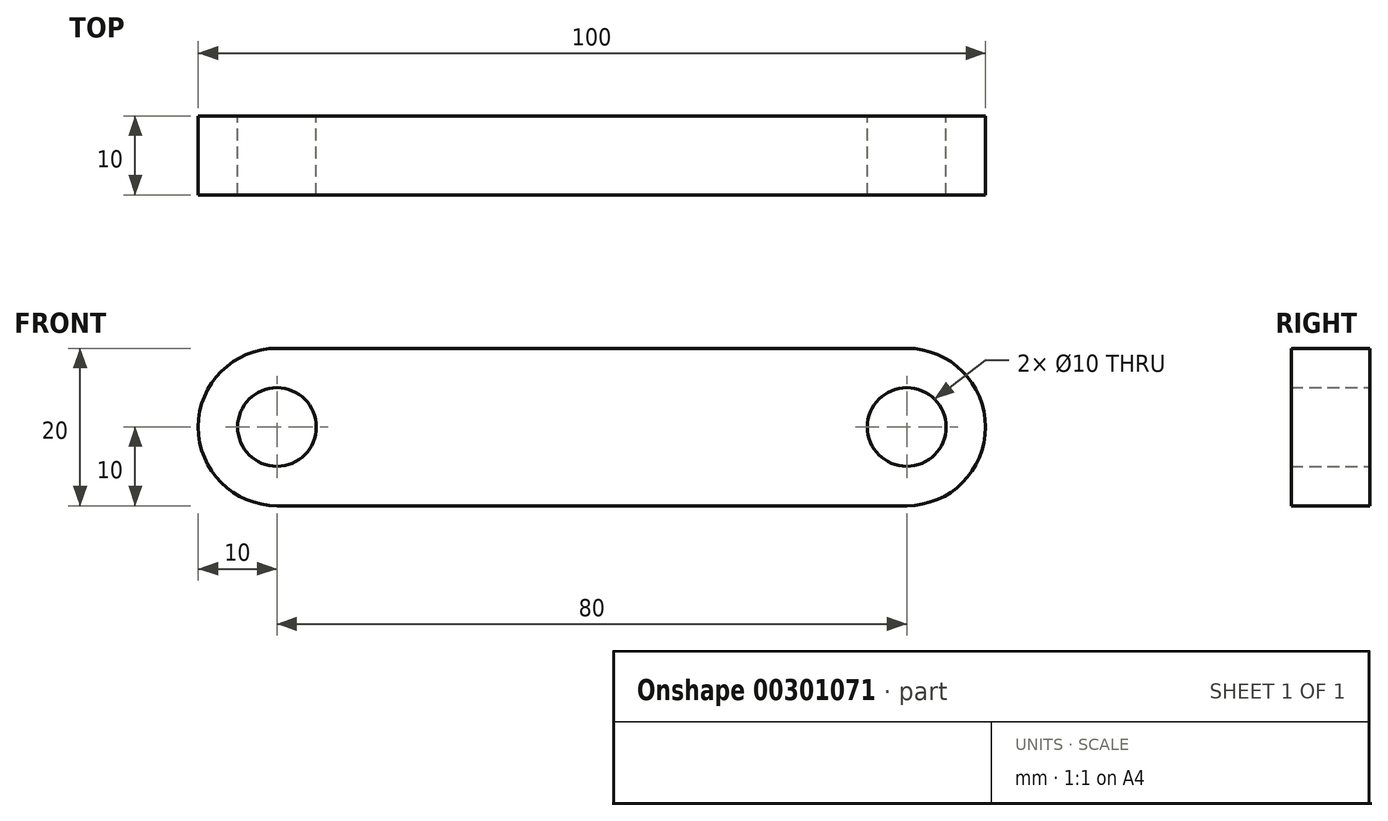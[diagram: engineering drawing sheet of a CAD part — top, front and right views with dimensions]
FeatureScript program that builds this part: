
annotation { "Feature Type Name" : "Feature", "Feature Type Description" : "" }
export const myFeature = defineFeature(function(context is Context, id is Id, definition is map)
    precondition{}
    {
        {
            var Q0;
            Q0=qCreatedBy(makeId("Front.planeOp"),FACE);
            var sketch = newSketch(context, id + "F0", { "sketchPlane" : qUnion([Q0])});
            skLineSegment(sketch, "E0", {"start": v(0, 0) * mm, "end": v(80, 0) * mm});
            skLineSegment(sketch, "E1", {"start": v(0, -20) * mm, "end": v(80, -20) * mm});
            skArc(sketch, "E2", {"start": v(0, 0) * mm, "mid": v(-10, -10) * mm, "end": v(0, -20) * mm});
            skArc(sketch, "E3", {"start": v(80, 0) * mm, "mid": v(90, -10) * mm, "end": v(80, -20) * mm});
            skCircle(sketch, "E4", {"center": v(0, -10) * mm, "radius": 5 * mm});
            skCircle(sketch, "E5", {"center": v(80, -10) * mm, "radius": 5 * mm});
            skLineSegment(sketch, "E6", {"start": v(0, -10) * mm, "end": v(80, -10) * mm, "construction": true});
            skSolve(sketch);
        }
        {
            var Q0;
            Q0=makeQuery(id+"F0.imprint","IMPRINT",FACE,{"disambiguationData":[TD([[makeQuery(id+"F0.imprint","IMPRINT",EDGE,{"derivedFrom":sQuery(id+"F0.wireOp",EDGE,"E0")}),-1.0]])]});
            extrude(context, id + "F1", {"entities" : qUnion([Q0]), "depth" : 10 * mm});
        }
    });
